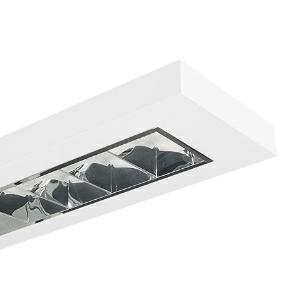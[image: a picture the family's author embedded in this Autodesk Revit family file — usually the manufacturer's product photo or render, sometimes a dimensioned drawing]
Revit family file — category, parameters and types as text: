
# Revit family: 3f_filippi_-_3f_travetta_2mg_3f_filippi_-_11516_-_3f_travetta_led_2x22w-940_dali_2mg_l1590
name_source: partatom
category: Lighting Fixtures
units: mm (PartAtom-declared; Revit-internal decimal feet)

## family parameters
Cut with Voids When Loaded = No
Host = Face
Light Source = No
Part Type = Normal
Room Calculation Point = No
Round Connector Dimension = Use Diameter
Shared = No

## types (1)
- 3F Filippi - 3F Travetta 2MG (1 x LED, 4833 lm, 49 W, 4000 K)
    Apparent Load = 49 VA
    Approval mark = ENEC
    CIE Flux Codes = 72 99 100 100 100
    Color Rendering = 90
    Color Temperature = 4000 K
    Control Gear = Electronic transformer
    Default Elevation = 1800 mm
    Description = ILLUMINOTECHNICAL
Luminous efficiency 100% (DLOR 100%, ULOR 0%).
Initial luminous flux of the luminaire 4833 lm.
Direct symmetric distribution.
Installation Interdistance Transv.D = 1.29 x hu - Long.D = 1.23 x hu.
Average luminance <1000 cd/m² for radial angles >65°.
Tabular UGR (CIE 117 - 4H-8H; S=0.25H; 70/50/20): RUG 16.2 - 18.4.
Beam angle: 80° - 84°.
Luminous efficacy 99 lm/W.
Lifetime (L93/B10): 30000 h. (tq+25°C)
Lifetime (L90/B10): 50000 h. (tq+25°C)
Lifetime (L85/B10): 80000 h. (tq+25°C)
Lifetime (L80/B10): 100000 h. (tq+25°C)
Sudden decreased luminous flux after 50000 hours: 0% (C0).
Photobiological safety in compliance with IEC/TR 62778: RG0 risk exempt, (IEC 62471).
In compliance with IEC/EN 62722-2-1 - IEC/EN 62717 standards.

SOURCE
2 linear LED modules 22W/940.
Energy efficiency class (UE 2019/2020 - UE 2019/2015): E.
CIE 13.3 Colour rendering index: CRI >90 (R9 >50%).
IES TM-30 Fidelity Index: Rf = 92 Rg = 101.
CCT nominal colour temperature 4000 K.
Colour initial tolerance (MacAdam): SDCM 2.

MECHANICAL
Housing with squared shape in white painted galvannealed steel, with nonreflecting surface.
2MG parabolic louvre, high efficiency, in specular aluminium with superficial titanium-magnesium treatment, non-iridescent, with transverse blades closed at the top.
Prismatic flat diffuser in transparent methacrylate (PMMA), multilenticular, anti-glare, prismatic exterior, placed above louvre blades.
Film protective against dust and finger marks, adhesive, attached to louvre.
Luminaire with limited surface temperature. - D - (EN 60598-2-24)
Dimensions: 1590x190 mm, height 60 mm. Weight 5.22 kg.
IP20 protection degree.
Mechanical strength to impacts IK02 (0.2 joule).
Glow-wire test resistance 650°C.

ELECTRICAL
Halogen Free DALI-2 DATI (Parts 251, 252, 253), PUSH-DIM, electronic wiring 230V-50/60Hz, power factor 0.95 at full load, THD <25%, constant output current, SELV, class I, 1 driver, 1 DALI addresse.
Power of the luminaire 49 W.
CE - IEC 60598-1 - EN 60598-1.
SAFE FLICKER: PstLM=<1 and SVM=<0.4 (IEC TR 61547-1 and IEC TR 63158), to ensure a more comfortable and safe light.
Luminaire compliant with EN 60598-2-22 for power supply from a centralised emergency system CPSS (Central Power Supply System), not incorporated in the luminaire - high risk areas excluded. The default power and flux are 100% in AC and 15% in DC.
Ambient temperature from 0°C to +25°C.
Temperature class T6 max 85°C.
5-pole terminal block for cascade line connection with connection capacity 2x2.5 mm².
Relative humidity UR: <85%.

INSTALLATION
Ceiling / Suspended.
All accessories dedicated to this product are available on the Catalog and on our website www.3F-Filippi.com.

APPLICATIONS
In environments, even with reduced height, requiring a comfortable light.
Exhibitions area, halls, great halls and shops.
In environments with VDTs, managerial offices and staterooms, public offices and schools.

LIGHT MANAGEMENT
Recommended minimum setting: 10%.
The luminaire, equipped with (DALI-2 DATI) driver, can be controlled manually with 3F Easy Dim technology or automatically/manually with wired or wireless DALI/D2D control systems.
The D2D driver guarantees interoperability with other devices with the same certification by making the following information available:
Device Data (Part 251), Energy Report (Part 252), Diagnosis & Maintenance (Part 253).
In electrical systems without a regulation system (manual or automatic) and DALI bus, a suitable jumper must be made on the DA-DA terminals of the appliance.

WARNING
Luminaire designed for disposal/recycling at end-of-life.
Replaceable (LED only) light source by a professional. Replaceable control gear by a professional.
    Height = 60 mm  [stored 0.19685 ft]
    Lamp = 1 x LED
    Lamp Light Flux = 4833 lm
    Lamp Power = 49 W
    Lamp count = 1
    Length = 1590 mm
    Lifetime = 50000 h
    Luminous efficacy = 99 lm/W
    Manufacturer = 3F Filippi
    ModVariant = No
    Model = 3F Filippi - 11516 - 3F Travetta LED 2x22W-940 DALI 2MG L1590
    Mounting Place = Ceiling
    Mounting Type = Pendant
    Number of Poles = 1
    OnlyDefault = Yes
    Power Factor = 1
    Product Name = 3F Filippi - 3F Travetta 2MG
    Product group = pendant luminaire
    ProductGroupID = 9
    Protection Class = Protection class I
    Protection Degree = IP 20
    RLX_Detail_Level = 1
    RLX_Emergency_Light_Flux = 0 lm
    RLX_Emergency_Type = 0
    RLX_Emergency_Type_DB = No
    RlxData = <blob elided: 57549 chars, md5=8b3bd42a>
    Socket = socket
    Standby Power = 0 W
    System Light Flux = 4833 lm
    System Power = 49 W
    Type Comments = Product without accessories
    Type Image = 3ffilippi_3f_travetta_led_2mg.jpg
    URL = http://relux.com
    VarID = ---
    Voltage = 0 V
    Weight = 0.00 kg
    Width = 190 mm  [stored 0.62336 ft]

note: [stored X ft] marks values corroborated as IEEE doubles in the binary element streams (Revit-internal decimal feet)

## geometry (parser evidence)
native form markers: Blend x4, Sweep x12
no freeform markers — native parametric forms only
